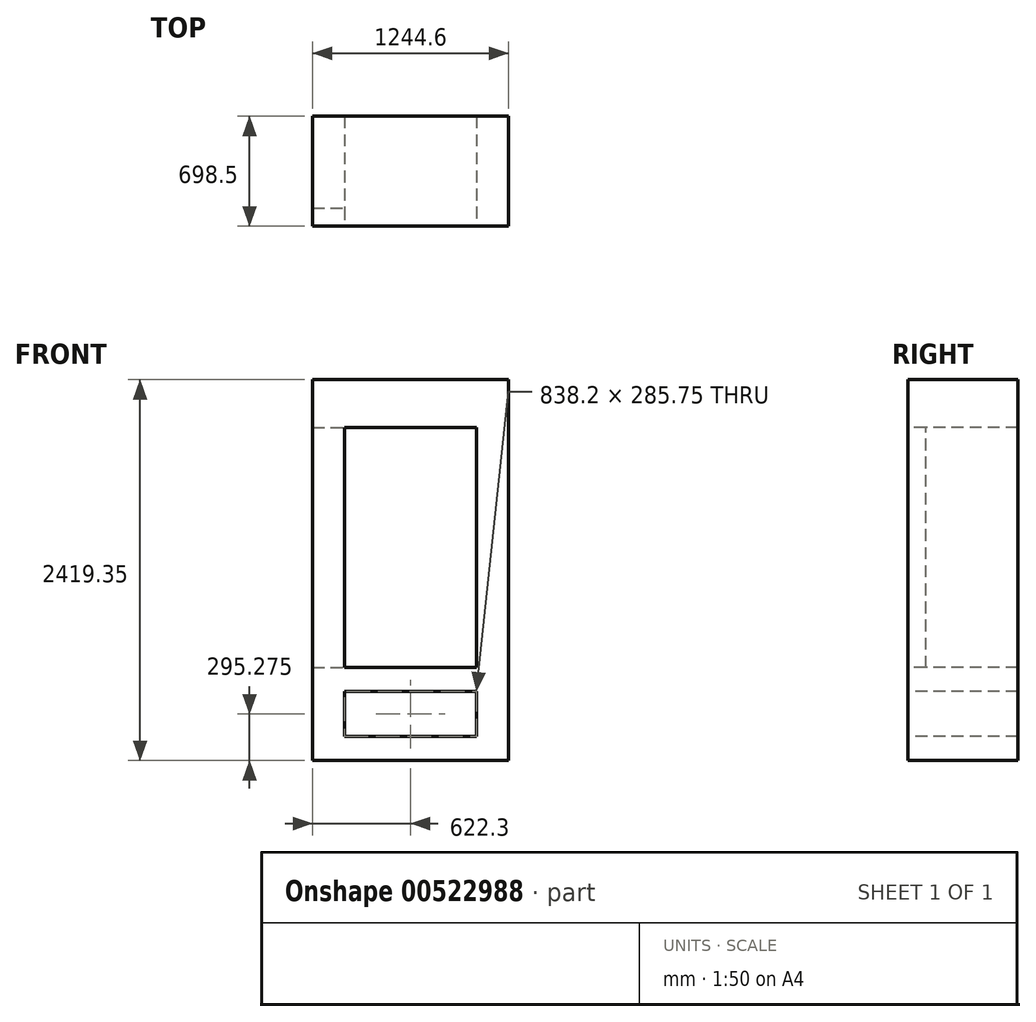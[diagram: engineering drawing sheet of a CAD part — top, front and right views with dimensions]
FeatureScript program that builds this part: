
annotation { "Feature Type Name" : "Feature", "Feature Type Description" : "" }
export const myFeature = defineFeature(function(context is Context, id is Id, definition is map)
    precondition{}
    {
        {
            var Q0;
            Q0=qCreatedBy(makeId("Top.planeOp"),FACE);
            var sketch = newSketch(context, id + "F0", { "sketchPlane" : qUnion([Q0])});
            skPoint(sketch, "E0.middle", {"position": v(0, 0) * mm});
            skLineSegment(sketch, "E1.bottom", {"start": v(-622.3, -349.25) * mm, "end": v(622.3, -349.25) * mm});
            skLineSegment(sketch, "E1.top", {"start": v(-622.3, 349.25) * mm, "end": v(622.3, 349.25) * mm});
            skLineSegment(sketch, "E1.left", {"start": v(-622.3, -349.25) * mm, "end": v(-622.3, 349.25) * mm});
            skLineSegment(sketch, "E1.right", {"start": v(622.3, -349.25) * mm, "end": v(622.3, 349.25) * mm});
            skSolve(sketch);
        }
        {
            var Q0;
            Q0=qCreatedBy(makeId("Right.planeOp"),FACE);
            var Q1;
            Q1=sQuery(id+"F0.wireOp",VERTEX,"E1.right.start");
            cPlane(context, id + "F1", {"entities" : qUnion([Q0, Q1]), "cplaneType" : CPlaneType.PLANE_POINT, "offset" : 0 * mm, "width" : 152.4 * mm, "height" : 152.4 * mm});
        }
        {
            var Q0;
            Q0 = qSketchRegion(id + "F0", true);
            extrude(context, id + "F2", {"entities" : qUnion([Q0]), "depth" : 2419.35 * mm, "offsetDistance" : 25.4 * mm});
        }
        {
            var Q0;
            Q0=makeQuery(id+"F2.opExtrude","SWEPT_FACE",FACE,{"disambiguationData":[OSD([sQuery(id+"F0.wireOp",EDGE,"E1.bottom")])]});
            var sketch = newSketch(context, id + "F3", { "sketchPlane" : qUnion([Q0])});
            skLineSegment(sketch, "E2.bottom", {"start": v(419.1, 2114.55) * mm, "end": v(-419.1, 2114.55) * mm});
            skLineSegment(sketch, "E2.top", {"start": v(419.1, 590.55) * mm, "end": v(-419.1, 590.55) * mm});
            skLineSegment(sketch, "E2.left", {"start": v(419.1, 2114.55) * mm, "end": v(419.1, 590.55) * mm});
            skLineSegment(sketch, "E2.right", {"start": v(-419.1, 2114.55) * mm, "end": v(-419.1, 590.55) * mm});
            skPoint(sketch, "E2.middle", {"position": v(0, 1352.55) * mm});
            skSolve(sketch);
        }
        {
            var Q0;
            Q0 = qSketchRegion(id + "F3", true);
            extrude(context, id + "F4", {"entities" : qUnion([Q0]), "operationType" : NewBodyOperationType.REMOVE, "oppositeDirection" : true, "depth" : 698.5 * mm, "offsetDistance" : 25.4 * mm});
        }
        {
            var Q0;
            Q0=makeQuery(id+"F4.boolean.opBoolean","COPY",FACE,{"derivedFrom":makeQuery(id+"F4.opExtrude","SWEPT_FACE",FACE,{"disambiguationData":[OSD([sQuery(id+"F3.wireOp",EDGE,"E2.right")])]})});
            var sketch = newSketch(context, id + "F5", { "sketchPlane" : qUnion([Q0])});
            skLineSegment(sketch, "E3.bottom", {"start": v(349.25, 590.55) * mm, "end": v(-234.95, 590.55) * mm});
            skLineSegment(sketch, "E3.top", {"start": v(349.25, 2114.55) * mm, "end": v(-234.95, 2114.55) * mm});
            skLineSegment(sketch, "E3.left", {"start": v(349.25, 590.55) * mm, "end": v(349.25, 2114.55) * mm});
            skLineSegment(sketch, "E3.right", {"start": v(-234.95, 590.55) * mm, "end": v(-234.95, 2114.55) * mm});
            skPoint(sketch, "E3.middle.positionSnap0", {"position": v(0, 590.55) * mm});
            skPoint(sketch, "E3.middle.positionSnap1", {"position": v(-349.25, 1352.55) * mm});
            skPoint(sketch, "E3.centerSnap0", {"position": v(0, 590.55) * mm});
            skPoint(sketch, "E3.centerSnap1", {"position": v(-349.25, 1352.55) * mm});
            skSolve(sketch);
        }
        {
            var Q0;
            Q0 = qSketchRegion(id + "F5", true);
            extrude(context, id + "F6", {"entities" : qUnion([Q0]), "operationType" : NewBodyOperationType.REMOVE, "oppositeDirection" : true, "depth" : 203.2 * mm, "offsetDistance" : 25.4 * mm});
        }
        {
            var Q0;
            Q0=makeQuery(id+"F2.opExtrude","SWEPT_FACE",FACE,{"disambiguationData":[OSD([sQuery(id+"F0.wireOp",EDGE,"E1.bottom")])]});
            var sketch = newSketch(context, id + "F7", { "sketchPlane" : qUnion([Q0])});
            skLineSegment(sketch, "E4.bottom", {"start": v(419.1, 152.4) * mm, "end": v(-419.1, 152.4) * mm});
            skLineSegment(sketch, "E4.top", {"start": v(419.1, 438.15) * mm, "end": v(-419.1, 438.15) * mm});
            skLineSegment(sketch, "E4.left", {"start": v(419.1, 152.4) * mm, "end": v(419.1, 438.15) * mm});
            skLineSegment(sketch, "E4.right", {"start": v(-419.1, 152.4) * mm, "end": v(-419.1, 438.15) * mm});
            skPoint(sketch, "E4.middle", {"position": v(0, 295.28) * mm});
            skPoint(sketch, "E4.middle.positionSnap0", {"position": v(0, 0) * mm});
            skPoint(sketch, "E4.centerSnap0", {"position": v(0, 0) * mm});
            skSolve(sketch);
        }
        {
            var Q0;
            Q0=makeQuery(id+"F7.imprint","IMPRINT",FACE,{"disambiguationData":[TD([[makeQuery(id+"F7.imprint","IMPRINT",EDGE,{"derivedFrom":sQuery(id+"F7.wireOp",EDGE,"E4.bottom")}),-1.0]])]});
            extrude(context, id + "F8", {"entities" : qUnion([Q0]), "operationType" : NewBodyOperationType.REMOVE, "oppositeDirection" : true, "depth" : 698.5 * mm, "offsetDistance" : 25.4 * mm});
        }
    });
